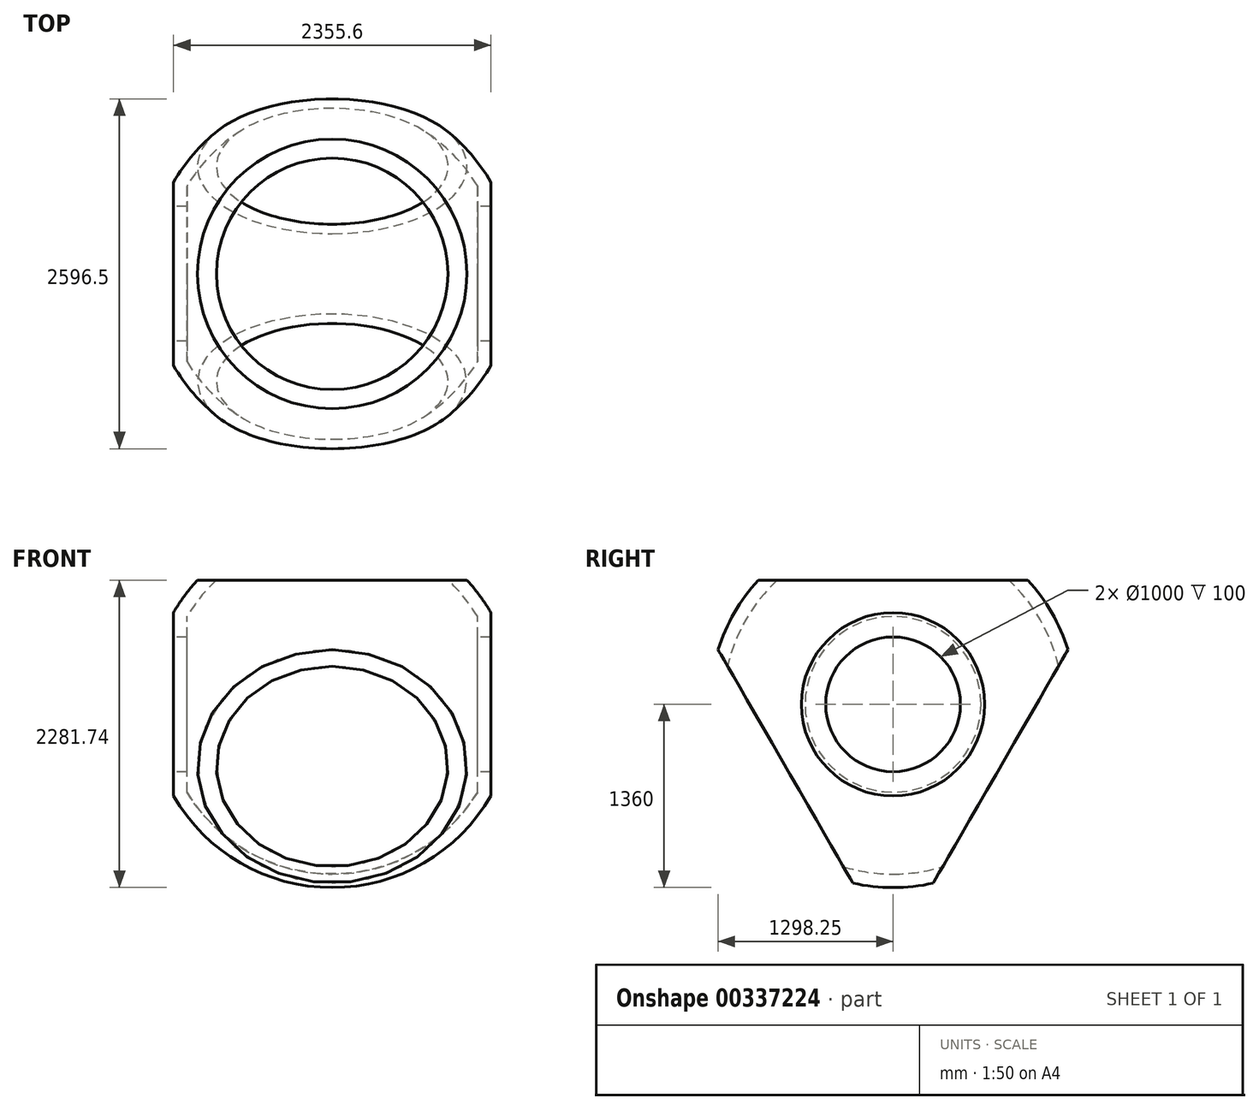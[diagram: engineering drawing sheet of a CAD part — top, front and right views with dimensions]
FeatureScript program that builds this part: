
annotation { "Feature Type Name" : "Feature", "Feature Type Description" : "" }
export const myFeature = defineFeature(function(context is Context, id is Id, definition is map)
    precondition{}
    {
        {
            var Q0;
            Q0=qCreatedBy(makeId("Front.planeOp"),FACE);
            var sketch = newSketch(context, id + "F0", { "sketchPlane" : qUnion([Q0])});
            skLineSegment(sketch, "E0", {"start": v(0, 1360) * mm, "end": v(0, 0) * mm, "construction": true});
            skLineSegment(sketch, "E1", {"start": v(1177.8, 680) * mm, "end": v(1177.8, 0) * mm});
            skLineSegment(sketch, "E2", {"start": v(-1360, 0) * mm, "end": v(1360, 0) * mm});
            skLineSegment(sketch, "E3.MirrorCS", {"start": v(-1177.8, 680) * mm, "end": v(-1177.8, 0) * mm});
            skCircle(sketch, "E4", {"center": v(0, 0) * mm, "radius": 1360 * mm});
            skSolve(sketch);
        }
        {
            var Q0;
            {var subQ0=sQuery(id+"F0.wireOp",EDGE,"E1");Q0=makeQuery(id+"F0.imprint","IMPRINT",FACE,{"disambiguationData":[TD([[makeQuery(id+"F0.imprint","IMPRINT",EDGE,{"derivedFrom":subQ0}),-1.0]])]});}
            var Q1;
            Q1=sQuery(id+"F0.wireOp",EDGE,"E2");
            revolve(context, id + "F1", {"entities" : qUnion([Q0]), "axis" : qUnion([Q1]), "revolveType" : RevolveType.FULL});
        }
        {
            var Q0;
            Q0=makeQuery(id+"F1.opRevolve","SWEPT_FACE",FACE,{"disambiguationData":[OSD([sQuery(id+"F0.wireOp",EDGE,"E3.MirrorCS")])]});
            var sketch = newSketch(context, id + "F2", { "sketchPlane" : qUnion([Q0])});
            skLineSegment(sketch, "E5", {"start": v(0, 0) * mm, "end": v(0, 921.74) * mm});
            skLineSegment(sketch, "E6.1.0", {"start": v(0, 0) * mm, "end": v(-798.25, -460.87) * mm});
            skLineSegment(sketch, "E6.2.0", {"start": v(0, 0) * mm, "end": v(798.25, -460.87) * mm});
            skPoint(sketch, "E6.center", {"position": v(0, 0) * mm});
            skLineSegment(sketch, "E7", {"start": v(-1000, 921.74) * mm, "end": v(1000, 921.74) * mm});
            skPoint(sketch, "E8", {"position": v(0, 921.74) * mm});
            skLineSegment(sketch, "E9.1.0", {"start": v(-298.25, -1326.9) * mm, "end": v(-1298.25, 405.16) * mm});
            skLineSegment(sketch, "E9.2.0", {"start": v(1298.25, 405.16) * mm, "end": v(298.25, -1326.9) * mm});
            skCircle(sketch, "E10", {"center": v(0, 0) * mm, "radius": 1360 * mm});
            skCircle(sketch, "E11", {"center": v(0, 0) * mm, "radius": 500 * mm});
            skSolve(sketch);
        }
        {
            var Q0;
            {var subQ0=sQuery(id+"F2.wireOp",EDGE,"E7");var subQ1=makeQuery(id+"F2.imprint","INTERSECT",VERTEX,{"derivedFrom":[sQuery(id+"F2.wireOp",EDGE,"E5"),subQ0]});Q0=makeQuery(id+"F2.imprint","IMPRINT",FACE,{"disambiguationData":[TD([[makeQuery(id+"F2.imprint","IMPRINT",EDGE,{"disambiguationData":[TD([[subQ1,1.0]])],"derivedFrom":subQ0}),1.0]])]});}
            var Q1;
            {var subQ0=sQuery(id+"F2.wireOp",EDGE,"E9.1.0");var subQ1=makeQuery(id+"F2.imprint","INTERSECT",VERTEX,{"derivedFrom":[sQuery(id+"F2.wireOp",EDGE,"E6.1.0"),subQ0]});Q1=makeQuery(id+"F2.imprint","IMPRINT",FACE,{"disambiguationData":[TD([[makeQuery(id+"F2.imprint","IMPRINT",EDGE,{"disambiguationData":[TD([[subQ1,1.0]])],"derivedFrom":subQ0}),1.0]])]});}
            var Q2;
            {var subQ0=sQuery(id+"F2.wireOp",EDGE,"E9.2.0");var subQ1=makeQuery(id+"F2.imprint","INTERSECT",VERTEX,{"derivedFrom":[sQuery(id+"F2.wireOp",EDGE,"E6.2.0"),subQ0]});Q2=makeQuery(id+"F2.imprint","IMPRINT",FACE,{"disambiguationData":[TD([[makeQuery(id+"F2.imprint","IMPRINT",EDGE,{"disambiguationData":[TD([[subQ1,1.0]])],"derivedFrom":subQ0}),1.0]])]});}
            extrude(context, id + "F3", {"entities" : qUnion([Q0, Q1, Q2]), "operationType" : NewBodyOperationType.REMOVE, "endBound" : BoundingType.THROUGH_ALL, "oppositeDirection" : true, "depth" : 25 * mm});
        }
        {
            var Q0;
            Q0=makeQuery(id+"F3.boolean.opBoolean","COPY",FACE,{"derivedFrom":makeQuery(id+"F3.opExtrude","SWEPT_FACE",FACE,{"disambiguationData":[OSD([sQuery(id+"F2.wireOp",EDGE,"E7")])]})});
            var Q1;
            Q1=makeQuery(id+"F3.boolean.opBoolean","COPY",FACE,{"derivedFrom":makeQuery(id+"F3.opExtrude","SWEPT_FACE",FACE,{"disambiguationData":[OSD([sQuery(id+"F2.wireOp",EDGE,"E9.2.0")])]})});
            var Q2;
            Q2=makeQuery(id+"F3.boolean.opBoolean","COPY",FACE,{"derivedFrom":makeQuery(id+"F3.opExtrude","SWEPT_FACE",FACE,{"disambiguationData":[OSD([sQuery(id+"F2.wireOp",EDGE,"E9.1.0")])]})});
            shell(context, id + "F4", {"entities" : qUnion([Q0, Q1, Q2]), "thickness" : 100 * mm});
        }
        {
            var Q0;
            {var subQ1=sQuery(id+"F2.wireOp",EDGE,"E5");var subQ3=sQuery(id+"F2.wireOp",EDGE,"E11");var subQ4=makeQuery(id+"F2.imprint","INTERSECT",VERTEX,{"derivedFrom":[subQ1,subQ3]});Q0=makeQuery(id+"F2.imprint","IMPRINT",FACE,{"disambiguationData":[TD([[makeQuery(id+"F2.imprint","IMPRINT",EDGE,{"disambiguationData":[TD([[subQ4,-1.0]])],"derivedFrom":subQ3}),1.0]])]});}
            var Q1;
            {var subQ1=sQuery(id+"F2.wireOp",EDGE,"E5");var subQ3=sQuery(id+"F2.wireOp",EDGE,"E11");var subQ4=makeQuery(id+"F2.imprint","INTERSECT",VERTEX,{"derivedFrom":[subQ1,subQ3]});Q1=makeQuery(id+"F2.imprint","IMPRINT",FACE,{"disambiguationData":[TD([[makeQuery(id+"F2.imprint","IMPRINT",EDGE,{"disambiguationData":[TD([[subQ4,1.0]])],"derivedFrom":subQ3}),1.0]])]});}
            var Q2;
            {var subQ1=sQuery(id+"F2.wireOp",EDGE,"E6.1.0");var subQ3=sQuery(id+"F2.wireOp",EDGE,"E11");var subQ4=makeQuery(id+"F2.imprint","INTERSECT",VERTEX,{"derivedFrom":[subQ1,subQ3]});Q2=makeQuery(id+"F2.imprint","IMPRINT",FACE,{"disambiguationData":[TD([[makeQuery(id+"F2.imprint","IMPRINT",EDGE,{"disambiguationData":[TD([[subQ4,-1.0]])],"derivedFrom":subQ3}),1.0]])]});}
            extrude(context, id + "F5", {"entities" : qUnion([Q0, Q1, Q2]), "operationType" : NewBodyOperationType.REMOVE, "endBound" : BoundingType.THROUGH_ALL, "oppositeDirection" : true, "depth" : 25 * mm});
        }
    });
